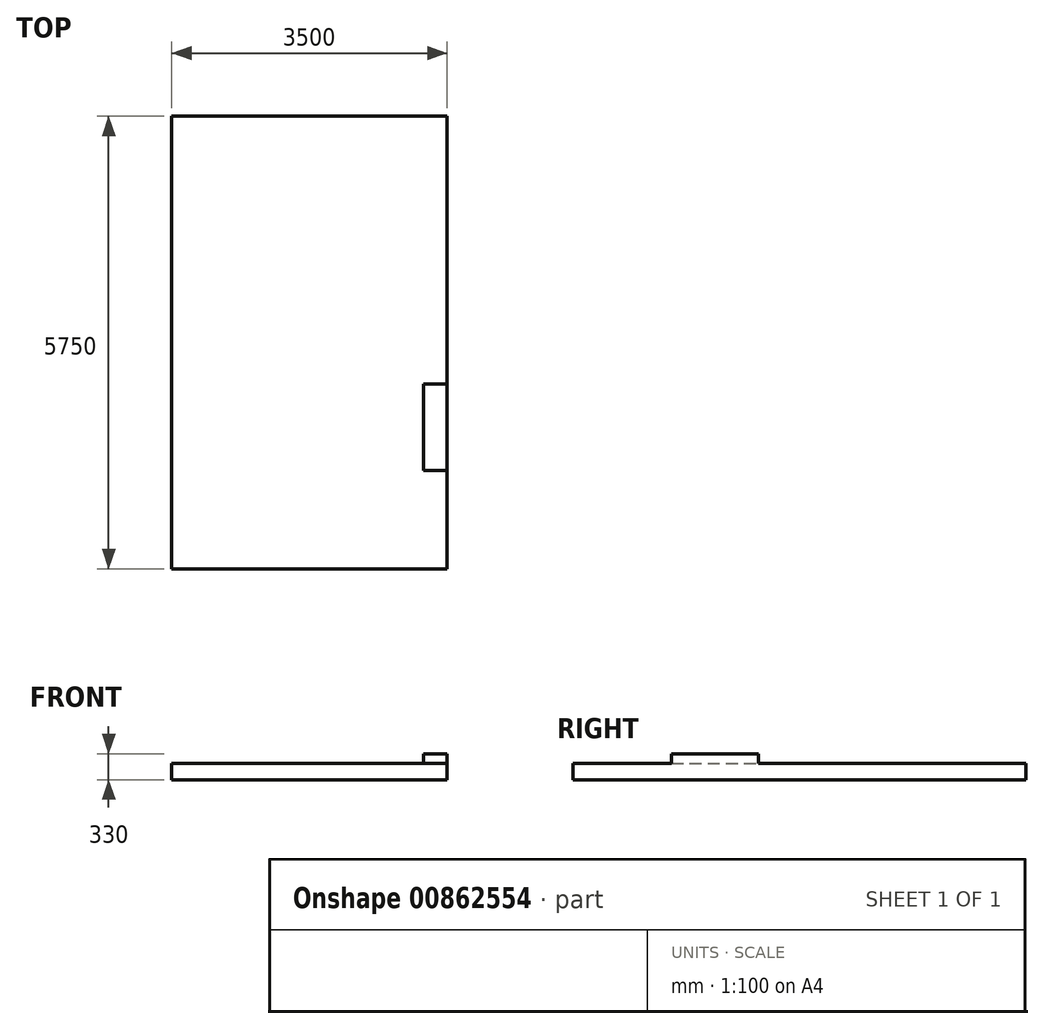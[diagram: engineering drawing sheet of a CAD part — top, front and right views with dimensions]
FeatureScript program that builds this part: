
annotation { "Feature Type Name" : "Feature", "Feature Type Description" : "" }
export const myFeature = defineFeature(function(context is Context, id is Id, definition is map)
    precondition{}
    {
        {
            var Q0;
            Q0=qCreatedBy(makeId("Top.planeOp"),FACE);
            var sketch = newSketch(context, id + "F0", { "sketchPlane" : qUnion([Q0])});
            skLineSegment(sketch, "E0.bottom", {"start": v(0, 0) * mm, "end": v(3500, 0) * mm});
            skLineSegment(sketch, "E0.top", {"start": v(0, 5750) * mm, "end": v(3500, 5750) * mm});
            skLineSegment(sketch, "E0.left", {"start": v(0, 0) * mm, "end": v(0, 5750) * mm});
            skLineSegment(sketch, "E0.right", {"start": v(3500, 0) * mm, "end": v(3500, 5750) * mm});
            skSolve(sketch);
        }
        {
            var Q0;
            Q0 = qSketchRegion(id + "F0", true);
            extrude(context, id + "F1", {"entities" : qUnion([Q0]), "depth" : 160 * mm, "offsetDistance" : 25 * mm});
        }
        {
            var Q0;
            Q0=makeQuery(id+"F1.opExtrude","CAP_FACE",FACE,{"disambiguationData":[OSD([sQuery(id+"F0.wireOp",EDGE,"E0.bottom"),sQuery(id+"F0.wireOp",EDGE,"E0.top"),sQuery(id+"F0.wireOp",EDGE,"E0.left"),sQuery(id+"F0.wireOp",EDGE,"E0.right")])],"isStart":false});
            var sketch = newSketch(context, id + "F2", { "sketchPlane" : qUnion([Q0])});
            skLineSegment(sketch, "E1.bottom", {"start": v(3500, 1250) * mm, "end": v(3200, 1250) * mm});
            skLineSegment(sketch, "E1.top", {"start": v(3500, 2350) * mm, "end": v(3200, 2350) * mm});
            skLineSegment(sketch, "E1.left", {"start": v(3500, 1250) * mm, "end": v(3500, 2350) * mm});
            skLineSegment(sketch, "E1.right", {"start": v(3200, 1250) * mm, "end": v(3200, 2350) * mm});
            skSolve(sketch);
        }
        {
            var Q0;
            Q0=makeQuery(id+"F2.imprint","IMPRINT",FACE,{"disambiguationData":[TD([[makeQuery(id+"F2.imprint","IMPRINT",EDGE,{"derivedFrom":sQuery(id+"F2.wireOp",EDGE,"E1.bottom")}),-1.0]])]});
            extrude(context, id + "F3", {"entities" : qUnion([Q0]), "operationType" : NewBodyOperationType.ADD, "depth" : 170 * mm, "offsetDistance" : 25 * mm});
        }
        {
            var Q0;
            Q0=makeQuery(id+"F1.opExtrude","SWEPT_FACE",FACE,{"disambiguationData":[OSD([sQuery(id+"F0.wireOp",EDGE,"E0.bottom")])]});
            var sketch = newSketch(context, id + "F4", { "sketchPlane" : qUnion([Q0])});
            skLineSegment(sketch, "E2.bottom", {"start": v(3500, 0) * mm, "end": v(3340, 0) * mm});
            skLineSegment(sketch, "E2.top", {"start": v(3500, 160) * mm, "end": v(3340, 160) * mm});
            skLineSegment(sketch, "E2.left", {"start": v(3500, 0) * mm, "end": v(3500, 160) * mm});
            skLineSegment(sketch, "E2.right", {"start": v(3340, 0) * mm, "end": v(3340, 160) * mm});
            skSolve(sketch);
        }
        {
            var Q0;
            Q0 = qSketchRegion(id + "F4", true);
            extrude(context, id + "F5", {"entities" : qUnion([Q0]), "operationType" : NewBodyOperationType.REMOVE, "endBound" : BoundingType.THROUGH_ALL, "oppositeDirection" : true, "depth" : 25 * mm, "offsetDistance" : 25 * mm});
        }
        {
            var Q0;
            Q0=makeQuery(id+"F1.opExtrude","SWEPT_FACE",FACE,{"disambiguationData":[OSD([sQuery(id+"F0.wireOp",EDGE,"E0.top")])]});
            var sketch = newSketch(context, id + "F6", { "sketchPlane" : qUnion([Q0])});
            skLineSegment(sketch, "E3.bottom", {"start": v(-3340, 0) * mm, "end": v(-3500, 0) * mm});
            skLineSegment(sketch, "E3.top", {"start": v(-3340, 160) * mm, "end": v(-3500, 160) * mm});
            skLineSegment(sketch, "E3.left", {"start": v(-3340, 0) * mm, "end": v(-3340, 160) * mm});
            skLineSegment(sketch, "E3.right", {"start": v(-3500, 0) * mm, "end": v(-3500, 160) * mm});
            skSolve(sketch);
        }
        {
            var Q0;
            Q0 = qSketchRegion(id + "F6", true);
            var Q1;
            Q1=makeQuery(id+"F1.opExtrude","SWEPT_FACE",FACE,{"disambiguationData":[OSD([sQuery(id+"F0.wireOp",EDGE,"E0.bottom")])]});
            extrude(context, id + "F7", {"entities" : qUnion([Q0]), "operationType" : NewBodyOperationType.ADD, "endBound" : BoundingType.UP_TO_SURFACE, "oppositeDirection" : true, "depth" : 5980 * mm, "endBoundEntityFace" : qUnion([Q1]), "offsetDistance" : 25 * mm});
        }
        {
            var Q0;
            Q0=makeQuery(id+"F1.opExtrude","CAP_FACE",FACE,{"disambiguationData":[OSD([sQuery(id+"F0.wireOp",EDGE,"E0.bottom"),sQuery(id+"F0.wireOp",EDGE,"E0.top"),sQuery(id+"F0.wireOp",EDGE,"E0.left"),sQuery(id+"F0.wireOp",EDGE,"E0.right")])],"isStart":false});
            var sketch = newSketch(context, id + "F8", { "sketchPlane" : qUnion([Q0])});
            skLineSegment(sketch, "E4.bottom", {"start": v(0, 0) * mm, "end": v(3340, 0) * mm});
            skLineSegment(sketch, "E4.top", {"start": v(0, 50) * mm, "end": v(3340, 50) * mm});
            skLineSegment(sketch, "E4.left", {"start": v(0, 0) * mm, "end": v(0, 50) * mm});
            skLineSegment(sketch, "E4.right", {"start": v(3340, 0) * mm, "end": v(3340, 50) * mm});
            skLineSegment(sketch, "E5", {"start": v(0, 2875) * mm, "end": v(3340, 2875) * mm, "construction": true});
            skLineSegment(sketch, "E6.MirrorCS", {"start": v(0, 5750) * mm, "end": v(3340, 5750) * mm});
            skLineSegment(sketch, "E7.MirrorCS", {"start": v(0, 5700) * mm, "end": v(3340, 5700) * mm});
            skSolve(sketch);
        }
        {
            var Q0;
            Q0 = qSketchRegion(id + "F8", true);
            var Q1;
            {var subQ0=sQuery(id+"F8.wireOp",EDGE,"E6.MirrorCS");Q1=makeQuery(id+"F8.imprint","IMPRINT",FACE,{"disambiguationData":[TD([[makeQuery(id+"F8.imprint","IMPRINT",EDGE,{"derivedFrom":subQ0}),-1.0]])]});}
            extrude(context, id + "F9", {"entities" : qUnion([Q0, Q1]), "operationType" : NewBodyOperationType.ADD, "depth" : 50 * mm, "offsetDistance" : 25 * mm});
        }
    });
